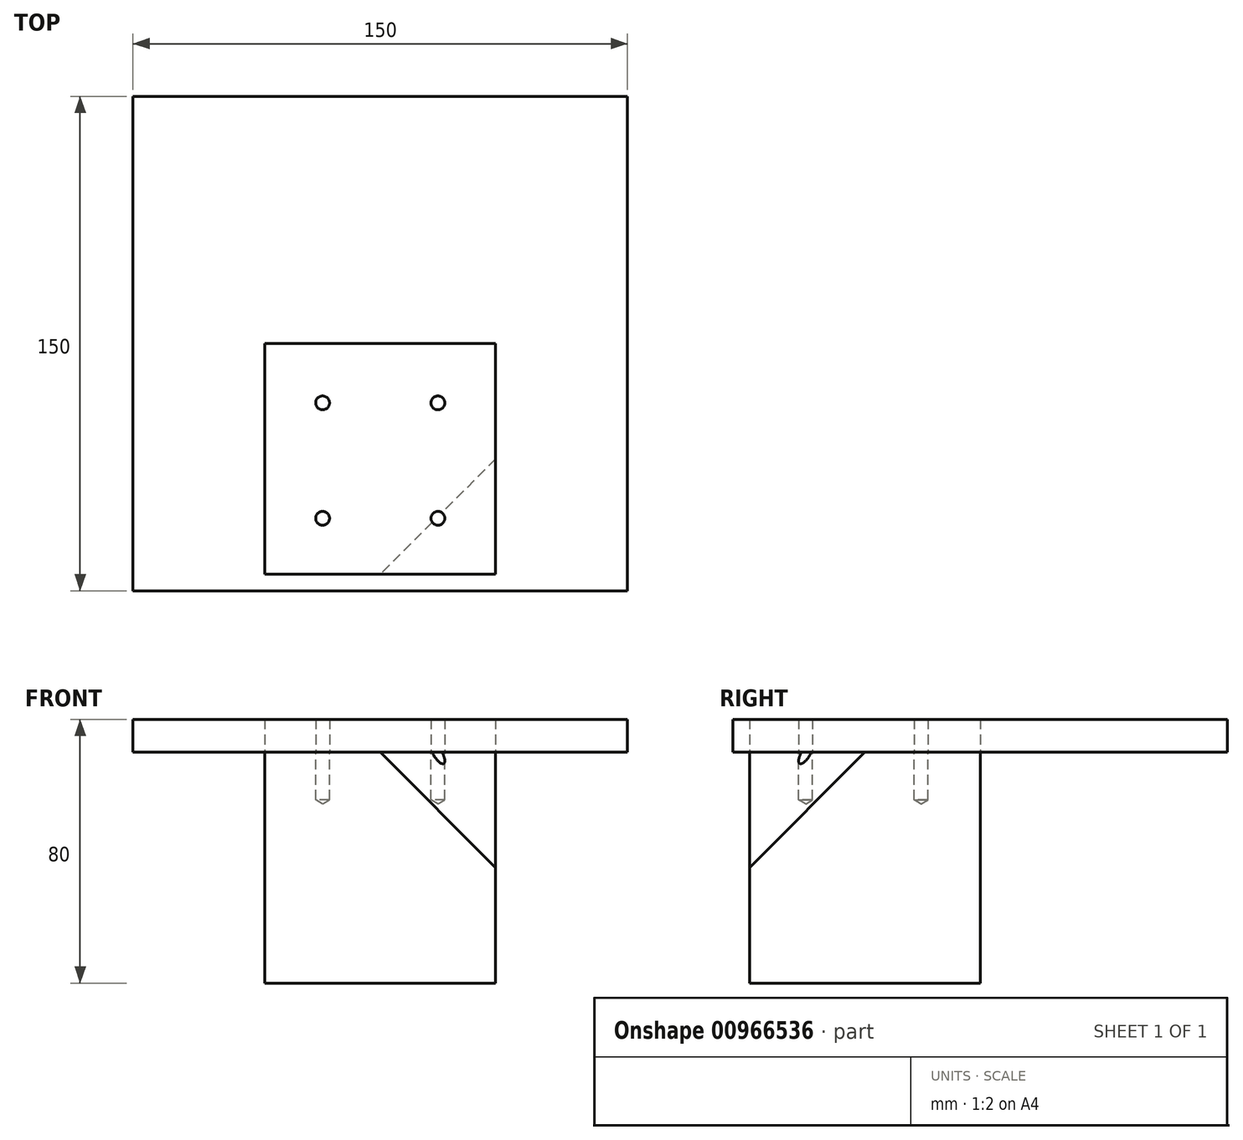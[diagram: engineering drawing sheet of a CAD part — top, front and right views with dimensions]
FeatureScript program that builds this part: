
annotation { "Feature Type Name" : "Feature", "Feature Type Description" : "" }
export const myFeature = defineFeature(function(context is Context, id is Id, definition is map)
    precondition{}
    {
        {
            var Q0;
            Q0=qCreatedBy(makeId("Front.planeOp"),FACE);
            var sketch = newSketch(context, id + "F0", { "sketchPlane" : qUnion([Q0])});
            skLineSegment(sketch, "E0.bottom", {"start": v(35, -35) * mm, "end": v(-35, -35) * mm});
            skLineSegment(sketch, "E0.top", {"start": v(35, 35) * mm, "end": v(-35, 35) * mm});
            skLineSegment(sketch, "E0.left", {"start": v(35, -35) * mm, "end": v(35, 35) * mm});
            skLineSegment(sketch, "E0.right", {"start": v(-35, -35) * mm, "end": v(-35, 35) * mm});
            skPoint(sketch, "E0.middle", {"position": v(0, 0) * mm});
            skSolve(sketch);
        }
        {
            var Q0;
            Q0=makeQuery(id+"F0.imprint","IMPRINT",FACE,{"disambiguationData":[TD([[makeQuery(id+"F0.imprint","IMPRINT",EDGE,{"derivedFrom":sQuery(id+"F0.wireOp",EDGE,"E0.bottom")}),-1.0]])]});
            extrude(context, id + "F1", {"entities" : qUnion([Q0]), "depth" : 70 * mm, "offsetDistance" : 25 * mm});
        }
        {
            var Q0;
            Q0=makeQuery(id+"F1.opExtrude","SWEPT_FACE",FACE,{"disambiguationData":[OSD([sQuery(id+"F0.wireOp",EDGE,"E0.top")])]});
            var sketch = newSketch(context, id + "F2", { "sketchPlane" : qUnion([Q0])});
            skPoint(sketch, "E1", {"position": v(-17.5, -18.01) * mm});
            skPoint(sketch, "E2", {"position": v(17.5, -18.01) * mm});
            skPoint(sketch, "E3", {"position": v(17.5, -53.01) * mm});
            skPoint(sketch, "E4", {"position": v(-17.5, -53.01) * mm});
            skSolve(sketch);
        }
        {
            var Q0;
            Q0=sQuery(id+"F2.wireOp",VERTEX,"E4");
            var Q1;
            Q1=sQuery(id+"F2.wireOp",VERTEX,"E1");
            var Q2;
            Q2=sQuery(id+"F2.wireOp",VERTEX,"E2");
            var Q3;
            Q3=sQuery(id+"F2.wireOp",VERTEX,"E3");
            var Q4;
            Q4=makeQuery(id+"F1.opExtrude","SWEPT_BODY",BODY,{"disambiguationData":[OSD([sQuery(id+"F0.wireOp",EDGE,"E0.bottom"),sQuery(id+"F0.wireOp",EDGE,"E0.top"),sQuery(id+"F0.wireOp",EDGE,"E0.left"),sQuery(id+"F0.wireOp",EDGE,"E0.right")])]});
            hole(context, id + "F3", {"style" : HoleStyle.SIMPLE, "endStyle" : HoleEndStyle.BLIND, "standardTappedOrClearance" : lookupTablePath({ "standard" : "ISO", "engagement" : "75%", "pitch" : "0.8 mm", "size" : "M5", "type" : "Tapped" }), "standardBlindInLast" : lookupTablePath({ "standard" : "ISO", "fit" : "Normal", "engagement" : "75%", "pitch" : "0.8 mm", "size" : "M5", "type" : "Clearance & tapped" }), "holeDiameter" : 4.2 * mm, "majorDiameter" : 5 * mm, "showTappedDepth" : true, "holeDepth" : 14.4 * mm, "isTappedThrough" : true, "tappedDepth" : 12 * mm, "tapClearance" : 3, "locations" : qUnion([Q0, Q1, Q2, Q3]), "scope" : qUnion([Q4])});
        }
        {
            var Q0;
            Q0=makeQuery(id+"F1.opExtrude","SWEPT_FACE",FACE,{"disambiguationData":[OSD([sQuery(id+"F0.wireOp",EDGE,"E0.top")])]});
            var sketch = newSketch(context, id + "F4", { "sketchPlane" : qUnion([Q0])});
            skPoint(sketch, "E5", {"position": v(0, -70) * mm});
            skPoint(sketch, "E6", {"position": v(35, -35) * mm});
            skSolve(sketch);
        }
        {
            var Q0;
            Q0=makeQuery(id+"F1.opExtrude","CAP_EDGE",EDGE,{"disambiguationData":[OSD([sQuery(id+"F0.wireOp",EDGE,"E0.left")])],"isStart":false});
            cPoint(context, id + "F5", {"entities" : qUnion([Q0]), "parameter" : 0.5});
        }
        {
            var Q0;
            Q0=sQuery(id+"F4.wireOp",VERTEX,"E5");
            var Q1;
            Q1=sQuery(id+"F4.wireOp",VERTEX,"E6");
            var Q2;
            Q2 = qCreatedBy(id + "F5" ,VERTEX);
            cPlane(context, id + "F6", {"entities" : qUnion([Q0, Q1, Q2]), "cplaneType" : CPlaneType.THREE_POINT, "offset" : 25 * mm, "width" : 150 * mm, "height" : 150 * mm});
        }
        {
            var Q0;
            Q0=qCreatedBy(id+"F6.planeOp",FACE);
            var sketch = newSketch(context, id + "F7", { "sketchPlane" : qUnion([Q0])});
            skLineSegment(sketch, "E7.bottom", {"start": v(-42.87, -49.5) * mm, "end": v(0, -49.5) * mm});
            skLineSegment(sketch, "E7.top", {"start": v(-42.87, 0) * mm, "end": v(0, 0) * mm});
            skLineSegment(sketch, "E7.left", {"start": v(-42.87, -49.5) * mm, "end": v(-42.87, 0) * mm});
            skLineSegment(sketch, "E7.right", {"start": v(0, -49.5) * mm, "end": v(0, 0) * mm});
            skSolve(sketch);
        }
        {
            var Q0;
            Q0=makeQuery(id+"F7.imprint","IMPRINT",FACE,{"disambiguationData":[TD([[makeQuery(id+"F7.imprint","IMPRINT",EDGE,{"derivedFrom":sQuery(id+"F7.wireOp",EDGE,"E7.bottom")}),1.0]])]});
            var Q1;
            Q1=makeQuery(id+"F1.opExtrude","CAP_VERTEX",VERTEX,{"disambiguationData":[OSD([sQuery(id+"F0.wireOp",EDGE,"E0.top"),sQuery(id+"F0.wireOp",EDGE,"E0.left")])],"isStart":false});
            extrude(context, id + "F8", {"entities" : qUnion([Q0]), "operationType" : NewBodyOperationType.REMOVE, "endBound" : BoundingType.UP_TO_VERTEX, "depth" : 25 * mm, "endBoundEntityVertex" : qUnion([Q1]), "offsetDistance" : 25 * mm});
        }
        {
            var Q0;
            {var subQ0=sQuery(id+"F0.wireOp",EDGE,"E0.top");Q0=makeQuery(id+"F4.imprint","IMPRINT",FACE,{"disambiguationData":[TD([[makeQuery(id+"F4.imprint","IMPRINT",EDGE,{"derivedFrom":makeQuery(id+"F1.opExtrude","CAP_EDGE",EDGE,{"disambiguationData":[OSD([subQ0])],"isStart":true})}),1.0]])]});}
            var sketch = newSketch(context, id + "F9", { "sketchPlane" : qUnion([Q0])});
            skLineSegment(sketch, "E8.bottom", {"start": v(-75, -75) * mm, "end": v(75, -75) * mm});
            skLineSegment(sketch, "E8.top", {"start": v(-75, 75) * mm, "end": v(75, 75) * mm});
            skLineSegment(sketch, "E8.left", {"start": v(-75, -75) * mm, "end": v(-75, 75) * mm});
            skLineSegment(sketch, "E8.right", {"start": v(75, -75) * mm, "end": v(75, 75) * mm});
            skPoint(sketch, "E8.middle", {"position": v(0, 0) * mm});
            skSolve(sketch);
        }
        {
            var Q0;
            Q0=makeQuery(id+"F9.imprint","IMPRINT",FACE,{"disambiguationData":[TD([[makeQuery(id+"F9.imprint","IMPRINT",EDGE,{"derivedFrom":sQuery(id+"F9.wireOp",EDGE,"E8.bottom")}),1.0]])]});
            var Q1;
            {var subQ0=sQuery(id+"F0.wireOp",EDGE,"E0.top");Q1=makeQuery(id+"F4.imprint","IMPRINT",FACE,{"disambiguationData":[TD([[makeQuery(id+"F4.imprint","IMPRINT",EDGE,{"derivedFrom":makeQuery(id+"F1.opExtrude","CAP_EDGE",EDGE,{"disambiguationData":[OSD([subQ0])],"isStart":true})}),1.0]])]});}
            extrude(context, id + "F10", {"entities" : qUnion([Q0, Q1]), "depth" : 10 * mm, "offsetDistance" : 25 * mm});
        }
    });
